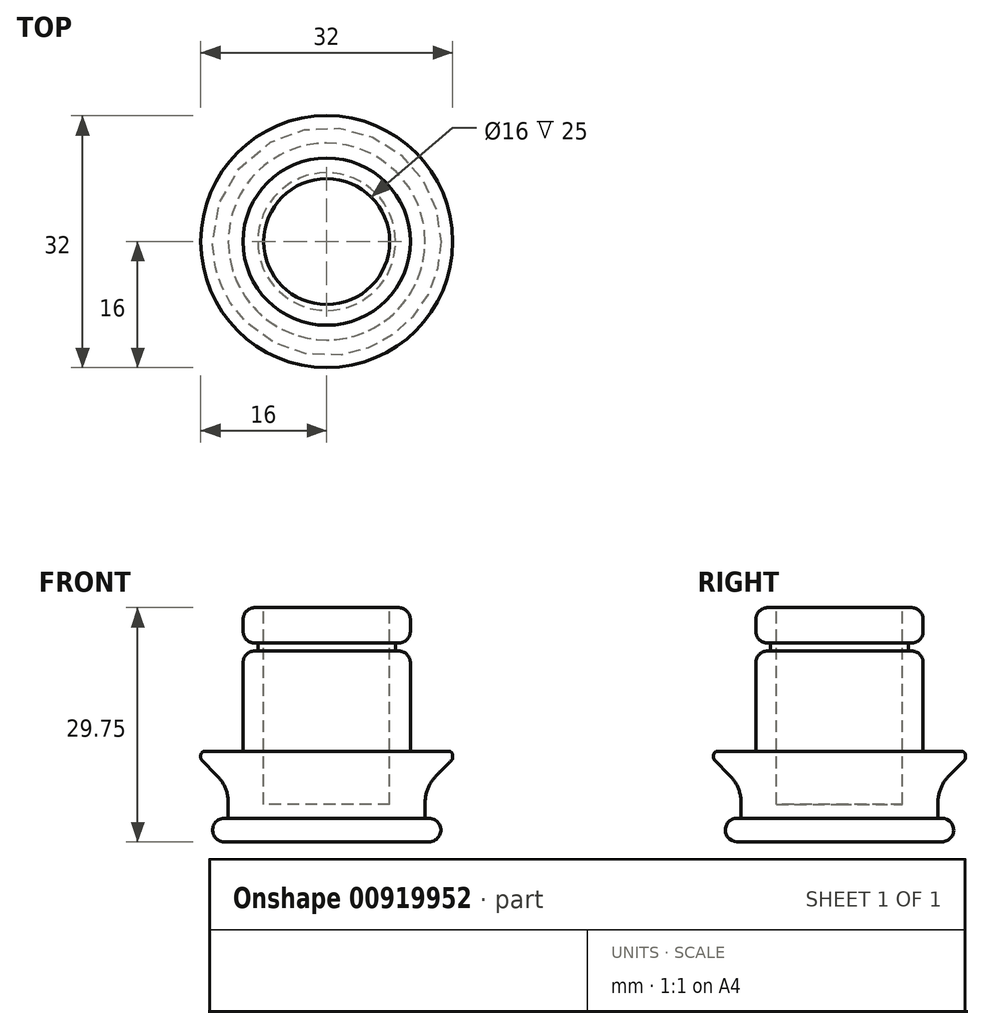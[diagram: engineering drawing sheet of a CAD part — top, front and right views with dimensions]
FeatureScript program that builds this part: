
annotation { "Feature Type Name" : "Feature", "Feature Type Description" : "" }
export const myFeature = defineFeature(function(context is Context, id is Id, definition is map)
    precondition{}
    {
        {
            var Q0;
            Q0=qCreatedBy(makeId("Top.planeOp"),FACE);
            var sketch = newSketch(context, id + "F0", { "sketchPlane" : qUnion([Q0])});
            skCircle(sketch, "E0", {"center": v(0, 0) * mm, "radius": 14.5 * mm});
            skSolve(sketch);
        }
        {
            var Q0;
            Q0 = qSketchRegion(id + "F0", true);
            extrude(context, id + "F1", {"entities" : qUnion([Q0]), "depth" : 3 * mm, "offsetDistance" : 25 * mm});
        }
        {
            var Q0;
            Q0=makeQuery(id+"F1.opExtrude","CAP_FACE",FACE,{"disambiguationData":[OSD([sQuery(id+"F0.wireOp",EDGE,"E0")])],"isStart":false});
            cPlane(context, id + "F2", {"entities" : qUnion([Q0]), "cplaneType" : CPlaneType.OFFSET, "offset" : 0 * mm, "width" : 150 * mm, "height" : 150 * mm});
        }
        {
            var Q0;
            Q0=qCreatedBy(id+"F2.planeOp",FACE);
            var sketch = newSketch(context, id + "F3", { "sketchPlane" : qUnion([Q0])});
            skCircle(sketch, "E1", {"center": v(0, 0) * mm, "radius": 12.5 * mm});
            skSolve(sketch);
        }
        {
            var Q0;
            Q0 = qSketchRegion(id + "F3", true);
            extrude(context, id + "F4", {"entities" : qUnion([Q0]), "operationType" : NewBodyOperationType.ADD, "depth" : 3.5 * mm, "offsetDistance" : 25 * mm});
        }
        {
            var Q0;
            Q0=makeQuery(id+"F4.opExtrude","CAP_FACE",FACE,{"disambiguationData":[OSD([sQuery(id+"F3.wireOp",EDGE,"E1")])],"isStart":false});
            cPlane(context, id + "F5", {"entities" : qUnion([Q0]), "cplaneType" : CPlaneType.OFFSET, "offset" : 0 * mm, "width" : 150 * mm, "height" : 150 * mm});
        }
        {
            var Q0;
            Q0=qCreatedBy(id+"F5.planeOp",FACE);
            var sketch = newSketch(context, id + "F6", { "sketchPlane" : qUnion([Q0])});
            skCircle(sketch, "E2", {"center": v(0, 0) * mm, "radius": 16 * mm});
            skSolve(sketch);
        }
        {
            var Q0;
            Q0 = qSketchRegion(id + "F6", true);
            extrude(context, id + "F7", {"entities" : qUnion([Q0]), "operationType" : NewBodyOperationType.ADD, "depth" : 5 * mm, "offsetDistance" : 25 * mm});
        }
        {
            var Q0;
            Q0=makeQuery(id+"F1.opExtrude","CAP_EDGE",EDGE,{"disambiguationData":[OSD([sQuery(id+"F0.wireOp",EDGE,"E0")])],"isStart":true});
            var Q1;
            Q1=makeQuery(id+"F1.opExtrude","CAP_EDGE",EDGE,{"disambiguationData":[OSD([sQuery(id+"F0.wireOp",EDGE,"E0")])],"isStart":false});
            fillet(context, id + "F8", {"entities" : qUnion([Q0, Q1]), "radius" : 1.5 * mm, "tangentPropagation" : true, "allowEdgeOverflow" : false});
        }
        {
            var Q0;
            Q0=makeQuery(id+"F7.opExtrude","CAP_EDGE",EDGE,{"disambiguationData":[OSD([sQuery(id+"F6.wireOp",EDGE,"E2")])],"isStart":true});
            chamfer(context, id + "F9", {"entities" : qUnion([Q0]), "width" : 4 * mm, "tangentPropagation" : true});
        }
        {
            var Q0;
            Q0=makeQuery(id+"F9.opChamfer","BLEND_EDGE",EDGE,{"blendedFrom":[makeQuery(id+"F7.opExtrude","CAP_EDGE",EDGE,{"disambiguationData":[OSD([sQuery(id+"F6.wireOp",EDGE,"E2")])],"isStart":true}),makeQuery(id+"F4.opExtrude","SWEPT_FACE",FACE,{"disambiguationData":[OSD([sQuery(id+"F3.wireOp",EDGE,"E1")])]})],"blendedInto":[makeQuery(id+"F4.opExtrude","SWEPT_FACE",FACE,{"disambiguationData":[OSD([sQuery(id+"F3.wireOp",EDGE,"E1")])]})]});
            fillet(context, id + "F10", {"entities" : qUnion([Q0]), "radius" : 5 * mm, "tangentPropagation" : true, "allowEdgeOverflow" : false});
        }
        {
            var Q0;
            {var subQ0=sQuery(id+"F6.wireOp",EDGE,"E2");Q0=makeQuery(id+"F9.opChamfer","BLEND_EDGE",EDGE,{"blendedFrom":[makeQuery(id+"F7.opExtrude","CAP_EDGE",EDGE,{"disambiguationData":[OSD([subQ0])],"isStart":true}),makeQuery(id+"F7.opExtrude","SWEPT_FACE",FACE,{"disambiguationData":[OSD([subQ0])]})],"blendedInto":[makeQuery(id+"F7.opExtrude","SWEPT_FACE",FACE,{"disambiguationData":[OSD([subQ0])]})]});}
            var Q1;
            Q1=makeQuery(id+"F7.opExtrude","CAP_EDGE",EDGE,{"disambiguationData":[OSD([sQuery(id+"F6.wireOp",EDGE,"E2")])],"isStart":false});
            fillet(context, id + "F11", {"entities" : qUnion([Q0, Q1]), "radius" : .5 * mm, "tangentPropagation" : true, "allowEdgeOverflow" : false});
        }
        {
            var Q0;
            Q0=makeQuery(id+"F7.opExtrude","CAP_FACE",FACE,{"disambiguationData":[OSD([sQuery(id+"F6.wireOp",EDGE,"E2")])],"isStart":false});
            cPlane(context, id + "F12", {"entities" : qUnion([Q0]), "cplaneType" : CPlaneType.OFFSET, "offset" : 0 * mm, "width" : 150 * mm, "height" : 150 * mm});
        }
        {
            var Q0;
            Q0=qCreatedBy(id+"F12.planeOp",FACE);
            var sketch = newSketch(context, id + "F13", { "sketchPlane" : qUnion([Q0])});
            skCircle(sketch, "E3", {"center": v(0, 0) * mm, "radius": 10.62 * mm});
            skSolve(sketch);
        }
        {
            var Q0;
            Q0 = qSketchRegion(id + "F13", true);
            extrude(context, id + "F14", {"entities" : qUnion([Q0]), "operationType" : NewBodyOperationType.ADD, "depth" : 12.75 * mm, "offsetDistance" : 25 * mm});
        }
        {
            var Q0;
            Q0=makeQuery(id+"F14.opExtrude","CAP_FACE",FACE,{"disambiguationData":[OSD([sQuery(id+"F13.wireOp",EDGE,"E3")])],"isStart":false});
            cPlane(context, id + "F15", {"entities" : qUnion([Q0]), "cplaneType" : CPlaneType.OFFSET, "offset" : (0) * mm, "width" : 150 * mm, "height" : 150 * mm});
        }
        {
            var Q0;
            Q0=qCreatedBy(id+"F15.planeOp",FACE);
            var sketch = newSketch(context, id + "F16", { "sketchPlane" : qUnion([Q0])});
            skCircle(sketch, "E4", {"center": v(0, 0) * mm, "radius": 8.75 * mm});
            skSolve(sketch);
        }
        {
            var Q0;
            Q0 = qSketchRegion(id + "F16", true);
            extrude(context, id + "F17", {"entities" : qUnion([Q0]), "operationType" : NewBodyOperationType.ADD, "depth" : 1 * mm, "offsetDistance" : 25 * mm});
        }
        {
            var Q0;
            Q0=makeQuery(id+"F17.opExtrude","CAP_FACE",FACE,{"disambiguationData":[OSD([sQuery(id+"F16.wireOp",EDGE,"E4")])],"isStart":false});
            cPlane(context, id + "F18", {"entities" : qUnion([Q0]), "cplaneType" : CPlaneType.OFFSET, "offset" : 0 * mm, "width" : 150 * mm, "height" : 150 * mm});
        }
        {
            var Q0;
            Q0=qCreatedBy(id+"F18.planeOp",FACE);
            var sketch = newSketch(context, id + "F19", { "sketchPlane" : qUnion([Q0])});
            skCircle(sketch, "E5", {"center": v(0, 0) * mm, "radius": 10.62 * mm});
            skSolve(sketch);
        }
        {
            var Q0;
            Q0 = qSketchRegion(id + "F19", true);
            extrude(context, id + "F20", {"entities" : qUnion([Q0]), "operationType" : NewBodyOperationType.ADD, "depth" : 4.5 * mm, "offsetDistance" : 25 * mm});
        }
        {
            var Q0;
            Q0=makeQuery(id+"F14.opExtrude","CAP_EDGE",EDGE,{"disambiguationData":[OSD([sQuery(id+"F13.wireOp",EDGE,"E3")])],"isStart":false});
            var Q1;
            Q1=makeQuery(id+"F20.opExtrude","CAP_EDGE",EDGE,{"disambiguationData":[OSD([sQuery(id+"F19.wireOp",EDGE,"E5")])],"isStart":true});
            var Q2;
            Q2=makeQuery(id+"F20.opExtrude","CAP_EDGE",EDGE,{"disambiguationData":[OSD([sQuery(id+"F19.wireOp",EDGE,"E5")])],"isStart":false});
            fillet(context, id + "F21", {"entities" : qUnion([Q0, Q1, Q2]), "radius" : 1.5 * mm, "tangentPropagation" : true, "allowEdgeOverflow" : false});
        }
        {
            var Q0;
            Q0=makeQuery(id+"F20.opExtrude","CAP_FACE",FACE,{"disambiguationData":[OSD([sQuery(id+"F19.wireOp",EDGE,"E5")])],"isStart":false});
            cPlane(context, id + "F22", {"entities" : qUnion([Q0]), "cplaneType" : CPlaneType.OFFSET, "offset" : 0 * mm, "width" : 150 * mm, "height" : 150 * mm});
        }
        {
            var Q0;
            Q0=qCreatedBy(id+"F22.planeOp",FACE);
            var sketch = newSketch(context, id + "F23", { "sketchPlane" : qUnion([Q0])});
            skCircle(sketch, "E6", {"center": v(0, 0) * mm, "radius": 8 * mm});
            skSolve(sketch);
        }
        {
            var Q0;
            Q0 = qSketchRegion(id + "F23", true);
            extrude(context, id + "F24", {"entities" : qUnion([Q0]), "operationType" : NewBodyOperationType.REMOVE, "oppositeDirection" : true, "depth" : 25 * mm, "offsetDistance" : 25 * mm});
        }
    });
